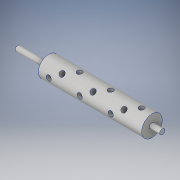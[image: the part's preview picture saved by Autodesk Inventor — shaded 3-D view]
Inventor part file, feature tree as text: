
AUTODESK INVENTOR PART (.ipt)
format: ipt  version: 2019 (Build 230136000, 136)  size: 162,816 bytes
history: native  units: in
note: dims shown in document units (in); Inventor stores cm internally (conversion verified against a paired STEP export)
features: sketch x5, plane x4, hole x3, revolve x1, pattern_linear x1, extrude x1, projected_geometry x1
ambient origin geometry x8: Origin, YZ Plane, XZ Plane, XY Plane, X Axis, Y Axis, Z Axis, Center Point
bodies: Solid1 (feature_tree)
feature tree (16):
  revolve  "Revolution1"  [1 undecoded]
  plane  "Work Plane1"
  hole  "Hole1"  [1 undecoded]
  plane  "Work Plane3"
  hole  "Hole2"  [1 undecoded]
  plane  "Work Plane4"
  hole  "Hole3"  [1 undecoded]
  pattern_linear  "Rectangular Pattern1"  Spacing1=1.0in  [1 undecoded]
  extrude  "Extrusion1"  Depth=1.5in
  sketch  "Sketch1"  dims[d0=0.25in d1=1.0in]
  sketch  "Sketch2"  dims[d2=1.5in d3=1.5in]
  plane  "Work Plane2"
  sketch  "Sketch3"  dims[d4=5.0in d5=90.0deg]
  sketch  "Sketch4"  dims[d6=0.5in]
  sketch  "Sketch5"  dims[d7=0.25in d8=0.75in d9=0.375in d10=0.25in d11=0.5635in d12=0.75in d13=0.8108in d14=45.0deg d15=1.0in d16=0.25in d17=0.75in d18=0.375in d19=0.25in d20=0.5635in d21=0.75in d22=0.8108in d23=1.5in d24=0.25in d25=0.75in d26=0.375in d27=0.25in d28=0.5635in d29=0.75in d30=0.8108in d31=1.1811in d33=1.5in d34=1.0in d35=0.0in]
  projected_geometry  "Projected Loop1"
note: 5 required parameter values undecoded (feature->parameter linkage not recoverable at this tier; creation-order binding heuristic only, values carry confidence <= 0.55)